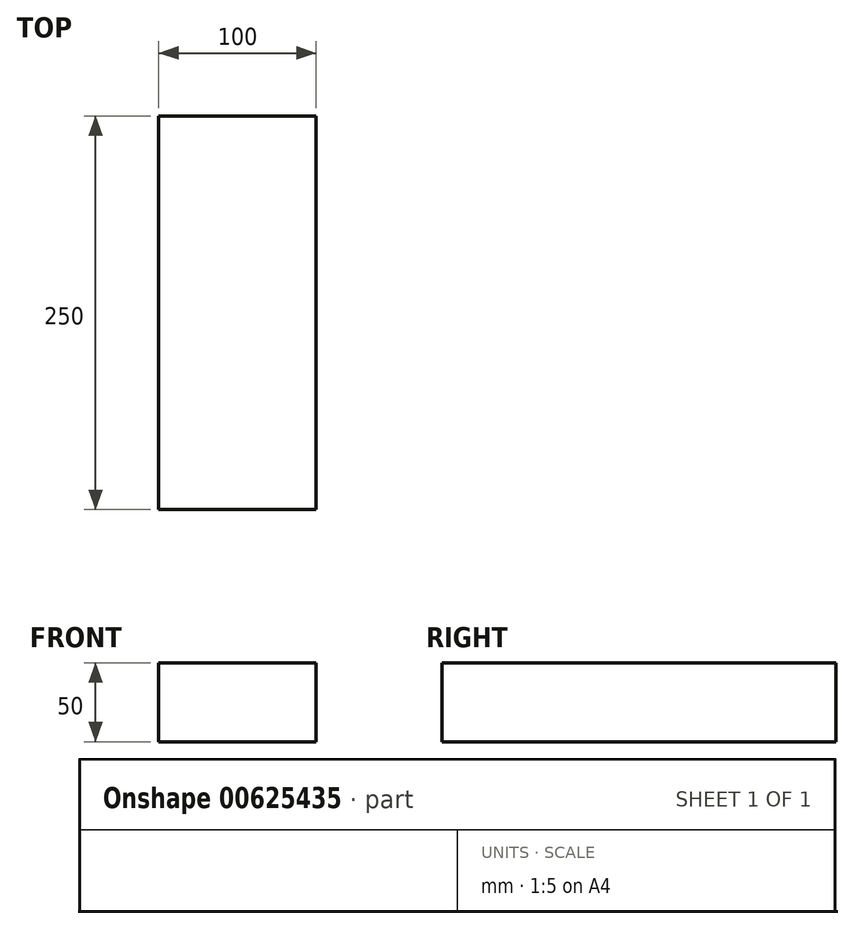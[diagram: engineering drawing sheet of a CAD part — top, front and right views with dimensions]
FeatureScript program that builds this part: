
annotation { "Feature Type Name" : "Feature", "Feature Type Description" : "" }
export const myFeature = defineFeature(function(context is Context, id is Id, definition is map)
    precondition{}
    {
        {
            var Q0;
            Q0=qCreatedBy(makeId("Front.planeOp"),FACE);
            var sketch = newSketch(context, id + "F0", { "sketchPlane" : qUnion([Q0])});
            skLineSegment(sketch, "E0.bottom", {"start": v(0, 0) * mm, "end": v(100, 0) * mm});
            skLineSegment(sketch, "E0.top", {"start": v(0, 50) * mm, "end": v(100, 50) * mm});
            skLineSegment(sketch, "E0.left", {"start": v(0, 0) * mm, "end": v(0, 50) * mm});
            skLineSegment(sketch, "E0.right", {"start": v(100, 0) * mm, "end": v(100, 50) * mm});
            skSolve(sketch);
        }
        {
            var Q0;
            Q0 = qSketchRegion(id + "F0", true);
            extrude(context, id + "F1", {"entities" : qUnion([Q0]), "depth" : 250 * mm, "offsetDistance" : 25 * mm});
        }
    });
